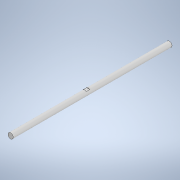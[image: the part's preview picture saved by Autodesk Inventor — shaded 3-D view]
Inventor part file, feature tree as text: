
AUTODESK INVENTOR PART (.ipt)
format: ipt  version: 2021 (Build 250183000, 183)  size: 102,400 bytes
history: native  units: in
note: dims shown in document units (in); Inventor stores cm internally (conversion verified against a paired STEP export)
features: extrude x2, sketch x2, other x1, plane x1
ambient origin geometry x8: Origin, YZ Plane, XZ Plane, XY Plane, X Axis, Y Axis, Z Axis, Center Point
bodies: Body1 (feature_tree)
feature tree (6):
  other  "Sólido1"
  extrude  "Extrusión1"  Depth=17.7165in TaperAngle=0.0deg
  plane  "Plano de trabajo1"
  extrude  "Extrusión4"  Depth=0.3937in
  sketch  "Boceto1"  dims[d0=0.5906in d1=17.7165in d2=0.0in]
  sketch  "Boceto5"  dims[d9=0.1969in d10=0.5906in d11=0.0591in d12=0.3937in d13=0.0in]
